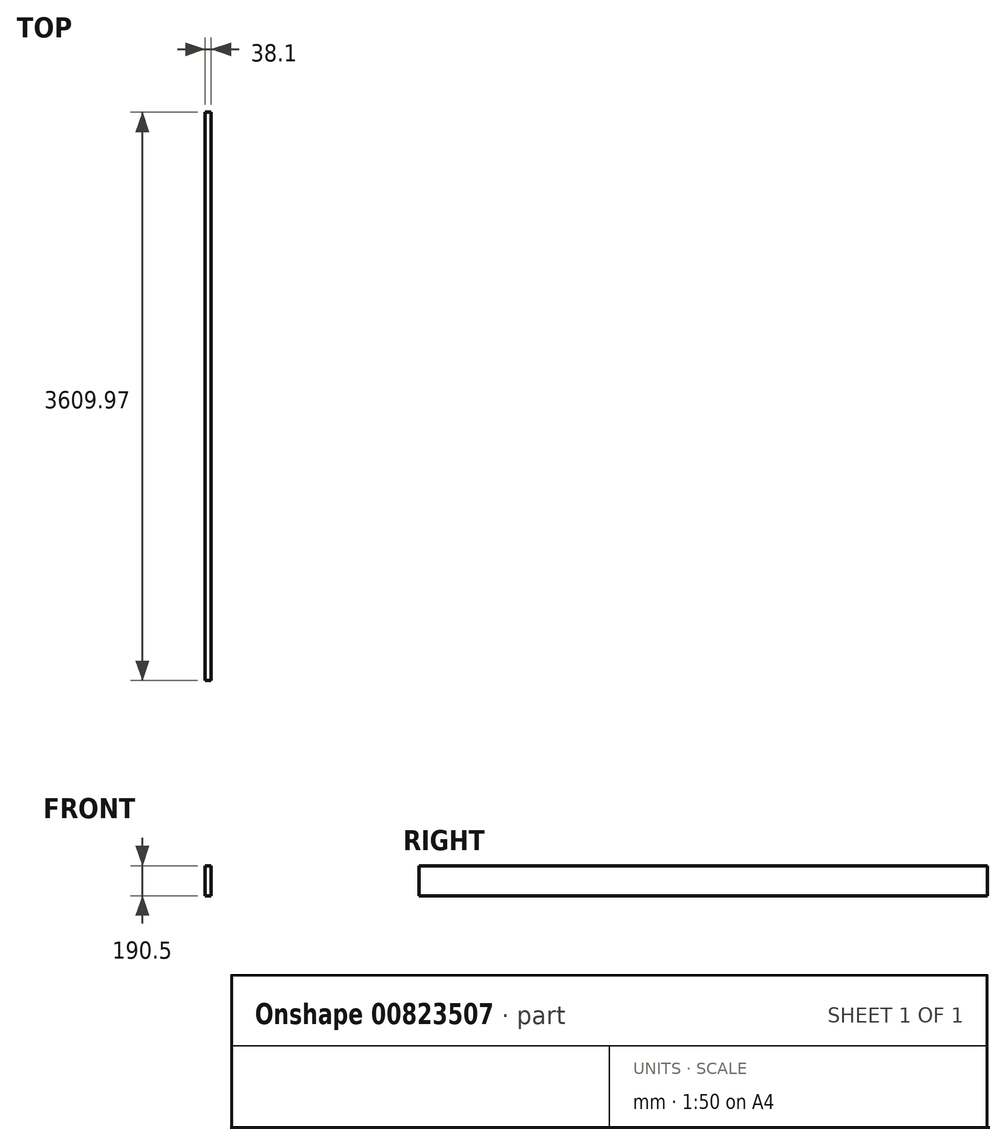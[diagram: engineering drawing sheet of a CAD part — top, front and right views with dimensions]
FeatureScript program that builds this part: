
annotation { "Feature Type Name" : "Feature", "Feature Type Description" : "" }
export const myFeature = defineFeature(function(context is Context, id is Id, definition is map)
    precondition{}
    {
        {
            var Q0;
            Q0=qCreatedBy(makeId("Front.planeOp"),FACE);
            var sketch = newSketch(context, id + "F0", { "sketchPlane" : qUnion([Q0])});
            skLineSegment(sketch, "E0.bottom", {"start": v(0, 0) * mm, "end": v(38.1, 0) * mm});
            skLineSegment(sketch, "E0.top", {"start": v(0, 190.5) * mm, "end": v(38.1, 190.5) * mm});
            skLineSegment(sketch, "E0.left", {"start": v(0, 0) * mm, "end": v(0, 190.5) * mm});
            skLineSegment(sketch, "E0.right", {"start": v(38.1, 0) * mm, "end": v(38.1, 190.5) * mm});
            skSolve(sketch);
        }
        {
            var Q0;
            Q0=qSketchRegion(id+"F0",true);
            extrude(context, id + "F1", {"entities" : qUnion([Q0]), "depth" : 3609.97 * mm, "offsetDistance" : 25.4 * mm});
        }
    });
